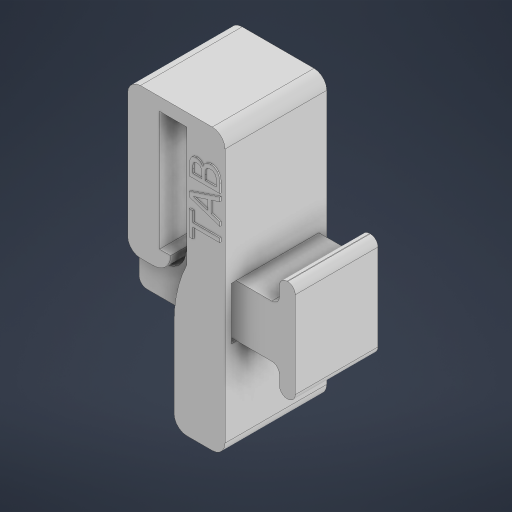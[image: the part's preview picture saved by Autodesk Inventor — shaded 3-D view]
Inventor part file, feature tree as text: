
AUTODESK INVENTOR PART (.ipt)
format: ipt  version: 2024.2 (Build 282272000, 272)  size: 392,704 bytes
history: native  units: in
note: dims shown in document units (in); Inventor stores cm internally (conversion verified against a paired STEP export)
features: extrude x6, fillet x4, thicken_offset x2, sketch x1
ambient origin geometry x8: Origin, YZ Plane, XZ Plane, XY Plane, X Axis, Y Axis, Z Axis, Center Point
bodies: Solid1 (feature_tree), Solid2 (feature_tree)
feature tree (13):
  sketch  "Sketch1"  dims[d0=0.215in d1=0.939in d2=0.027in d3=0.1in d4=0.8386in d5=0.25in d8=0.2306in d9=-0.0586in d10=0.25in d11=0.25in d12=0.1in d13=0.25in d14=0.3in d15=0.2in d16=0.4in d17=0.06in d18=0.0in d19=0.05in d20=0.0in d21=0.64in d22=0.0in d23=0.05in d24=0.0in d25=0.0669in d26=0.65in d27=0.0in d28=0.5in d29=0.01in d30=0.0in d31=0.002in d32=0.002in d33=0.002in d34=0.002in d35=1.0in d36=0.125in d37=0.8in d38=0.06in d39=0.06in d40=0.1in]
  extrude  "Extrusion1"  Depth=0.1in
  extrude  "Extrusion2"  Depth=0.1in
  extrude  "Extrusion3"  Depth=0.1in
  extrude  "Extrusion4"  Depth=0.1in
  extrude  "Extrusion5"  Depth=0.1in
  extrude  "Extrusion6"  Depth=0.1in
  thicken_offset  "Thicken1"
  thicken_offset  "Thicken2"
  fillet  "Fillet1"  [1 undecoded]
  fillet  "Fillet2"  Radius=0.25in
  fillet  "Fillet3"  Radius=0.25in
  fillet  "Fillet4"  Radius=0.1in
note: 1 required parameter value undecoded (feature->parameter linkage not recoverable at this tier; creation-order binding heuristic only, values carry confidence <= 0.55)
